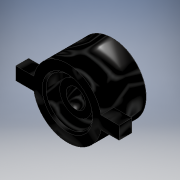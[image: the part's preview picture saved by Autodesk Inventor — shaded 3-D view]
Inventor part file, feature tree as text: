
AUTODESK INVENTOR PART (.ipt)
format: ipt  version: 2019 (Build 230136000, 136)  size: 151,552 bytes
history: native  units: mm
features: extrude x3, sketch x3, other x1, shell x1, fillet x1, chamfer x1
ambient origin geometry x8: Origin, YZ Plane, XZ Plane, XY Plane, X Axis, Y Axis, Z Axis, Center Point
bodies: Solide1 (feature_tree)
feature tree (10):
  other  "Button-SNES"
  extrude  "Extrusion1"  Depth=10.6mm
  shell  "Coque2"  Thickness=7.0mm
  extrude  "Extrusion4"  Depth=1.7mm
  extrude  "Extrusion5"  Depth=5.0mm
  fillet  "Congé3"  Radius=3.0mm
  chamfer  "Chanfrein1"  Distance=4.0mm
  sketch  "Esquisse1"
  sketch  "Esquisse6"
  sketch  "Esquisse7"
